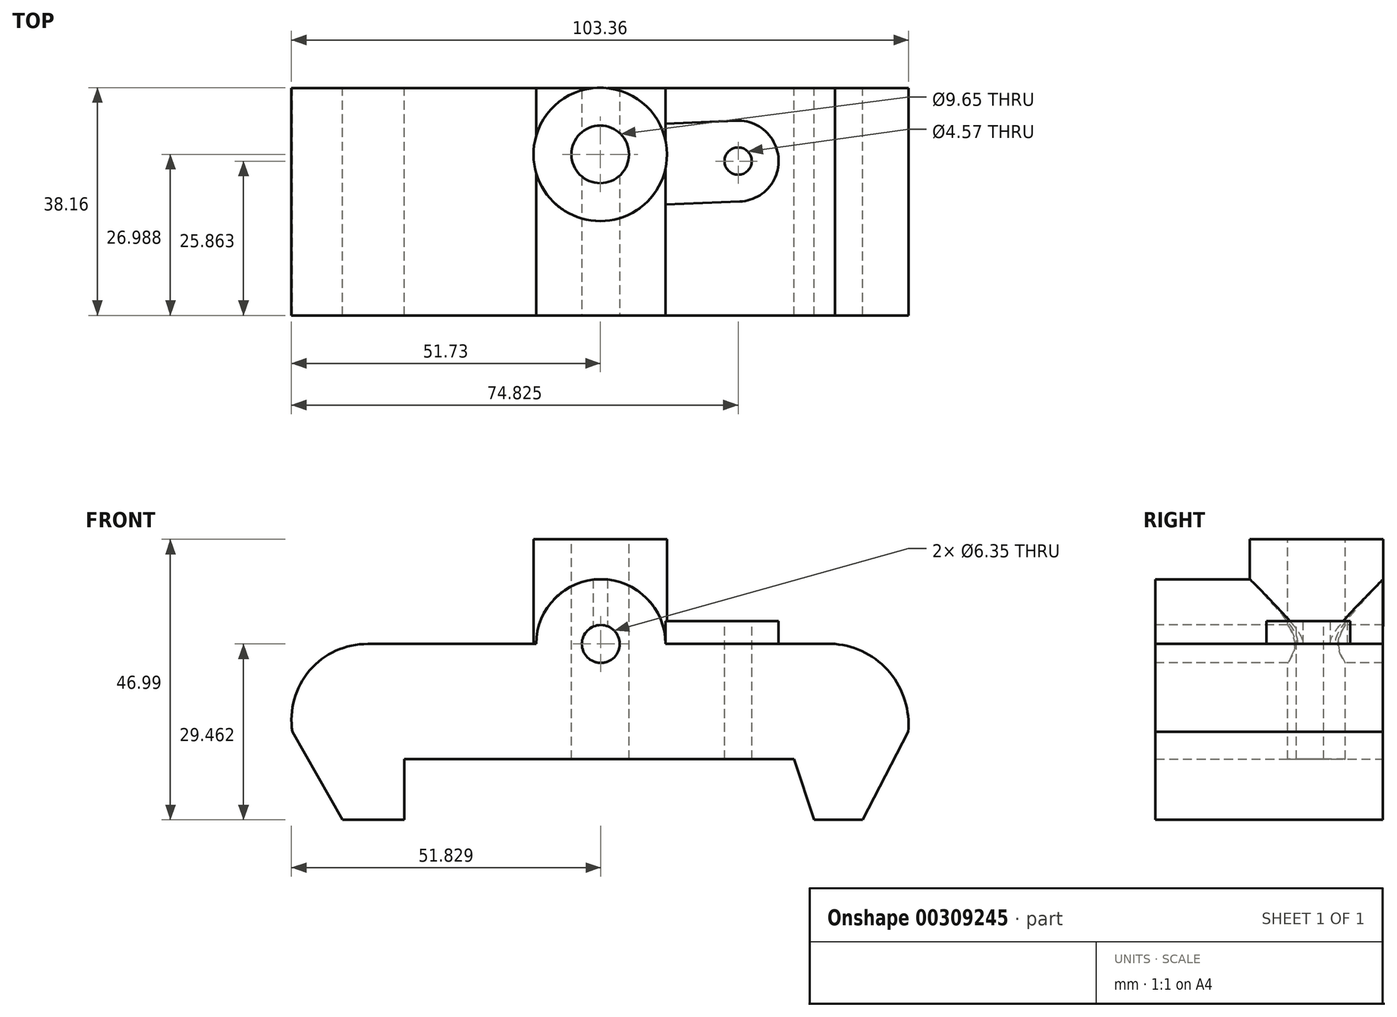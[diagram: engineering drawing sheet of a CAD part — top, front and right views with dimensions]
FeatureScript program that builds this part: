
annotation { "Feature Type Name" : "Feature", "Feature Type Description" : "" }
export const myFeature = defineFeature(function(context is Context, id is Id, definition is map)
    precondition{}
    {
        {
            var Q0;
            Q0=qCreatedBy(makeId("Front.planeOp"),FACE);
            var sketch = newSketch(context, id + "F0", { "sketchPlane" : qUnion([Q0])});
            skLineSegment(sketch, "E0.bottom", {"start": v(-43.18, -14.73) * mm, "end": v(-32.82, -14.73) * mm});
            skLineSegment(sketch, "E0.top", {"start": v(-39.11, 14.73) * mm, "end": v(-10.74, 14.73) * mm});
            skLineSegment(sketch, "E0.left", {"start": v(-51.56, 0) * mm, "end": v(-51.56, 4.06) * mm});
            skLineSegment(sketch, "E0.right", {"start": v(51.56, 0) * mm, "end": v(51.56, 2.62) * mm});
            skPoint(sketch, "E0.middle", {"position": v(0, 0) * mm});
            skArc(sketch, "E1", {"start": v(-38.94, 14.73) * mm, "mid": v(-48.67, 10.3) * mm, "end": v(-51.56, 0) * mm});
            skArc(sketch, "E2", {"start": v(51.56, 0) * mm, "mid": v(48.51, 9.92) * mm, "end": v(39.3, 14.73) * mm});
            skLineSegment(sketch, "E3", {"start": v(-51.56, 0) * mm, "end": v(-43.18, -14.73) * mm});
            skPoint(sketch, "E4.orphan", {"position": v(-51.56, 14.73) * mm});
            skPoint(sketch, "E5.orphan", {"position": v(-51.56, -14.73) * mm});
            skPoint(sketch, "E6.orphan", {"position": v(51.56, 14.73) * mm});
            skLineSegment(sketch, "E7", {"start": v(51.56, 0) * mm, "end": v(43.94, -14.73) * mm});
            skPoint(sketch, "E8.orphan", {"position": v(51.56, -14.73) * mm});
            skLineSegment(sketch, "E9.bottom", {"start": v(-32.82, -4.57) * mm, "end": v(32.46, -4.57) * mm});
            skLineSegment(sketch, "E9.left", {"start": v(-32.82, -4.57) * mm, "end": v(-32.82, -14.73) * mm});
            skPoint(sketch, "E10", {"position": v(-32.82, -14.73) * mm});
            skPoint(sketch, "E11", {"position": v(32.46, -14.73) * mm});
            skLineSegment(sketch, "E12.trimOffspring", {"start": v(35.81, -14.73) * mm, "end": v(43.94, -14.73) * mm});
            skLineSegment(sketch, "E13", {"start": v(32.46, -4.57) * mm, "end": v(35.81, -14.73) * mm});
            skArc(sketch, "E14", {"start": v(10.94, 14.73) * mm, "mid": v(0.1, 25.58) * mm, "end": v(-10.74, 14.73) * mm});
            skLineSegment(sketch, "E15.trimOffspring", {"start": v(10.94, 14.73) * mm, "end": v(39.3, 14.73) * mm});
            skSolve(sketch);
        }
        {
            var Q0;
            Q0 = qSketchRegion(id + "F0", true);
            extrude(context, id + "F1", {"entities" : qUnion([Q0]), "depth" : 38.1 * mm});
        }
        {
            var Q0;
            Q0=makeQuery(id+"F1.opExtrude","SWEPT_FACE",FACE,{"disambiguationData":[OSD([sQuery(id+"F0.wireOp",EDGE,"E0.top")])]});
            var sketch = newSketch(context, id + "F2", { "sketchPlane" : qUnion([Q0])});
            skCircle(sketch, "E16", {"center": v(0, -11.11) * mm, "radius": 11.18 * mm});
            skPoint(sketch, "E17", {"position": v(-24.84, -38.1) * mm});
            skSolve(sketch);
        }
        {
            var Q0;
            Q0 = qSketchRegion(id + "F2", true);
            extrude(context, id + "F3", {"entities" : qUnion([Q0]), "operationType" : NewBodyOperationType.ADD, "depth" : 17.53 * mm});
        }
        {
            var Q0;
            Q0=makeQuery(id+"F3.opExtrude","CAP_FACE",FACE,{"disambiguationData":[OSD([sQuery(id+"F2.wireOp",EDGE,"E16")])],"isStart":false});
            var sketch = newSketch(context, id + "F4", { "sketchPlane" : qUnion([Q0])});
            skPoint(sketch, "E18", {"position": v(0, -11.11) * mm});
            skSolve(sketch);
        }
        {
            var Q0;
            Q0=sQuery(id+"F4.wireOp",VERTEX,"E18");
            var Q1;
            Q1=makeQuery(id+"F1.opExtrude","SWEPT_BODY",BODY,{"disambiguationData":[OSD([sQuery(id+"F0.wireOp",EDGE,"E0.bottom"),sQuery(id+"F0.wireOp",EDGE,"E0.top"),sQuery(id+"F0.wireOp",EDGE,"E1"),sQuery(id+"F0.wireOp",EDGE,"E2"),sQuery(id+"F0.wireOp",EDGE,"E3"),sQuery(id+"F0.wireOp",EDGE,"E7"),sQuery(id+"F0.wireOp",EDGE,"E9.bottom"),sQuery(id+"F0.wireOp",EDGE,"E9.left"),sQuery(id+"F0.wireOp",EDGE,"E12.trimOffspring"),sQuery(id+"F0.wireOp",EDGE,"E13")])]});
            hole(context, id + "F5", {"style" : HoleStyle.SIMPLE, "endStyle" : HoleEndStyle.THROUGH, "holeDiameter" : 9.65 * mm, "tappedDepth" : 12.7 * mm, "tapClearance" : 3, "startFromSketch" : true, "locations" : qUnion([Q0]), "scope" : qUnion([Q1])});
        }
        {
            var Q0;
            Q0=makeQuery(id+"F1.opExtrude","SWEPT_FACE",FACE,{"disambiguationData":[OSD([sQuery(id+"F0.wireOp",EDGE,"E15.trimOffspring")])]});
            var sketch = newSketch(context, id + "F6", { "sketchPlane" : qUnion([Q0])});
            skArc(sketch, "E19", {"start": v(23.36, -19) * mm, "mid": v(29.86, -11.96) * mm, "end": v(22.8, -5.47) * mm});
            skLineSegment(sketch, "E20", {"start": v(22.8, -5.47) * mm, "end": v(10.94, -5.98) * mm});
            skLineSegment(sketch, "E21", {"start": v(23.36, -19) * mm, "end": v(10.94, -19.5) * mm});
            skSolve(sketch);
        }
        {
            var Q0;
            Q0=makeQuery(id+"F6.imprint","IMPRINT",FACE,{"disambiguationData":[TD([[makeQuery(id+"F6.imprint","IMPRINT",EDGE,{"derivedFrom":sQuery(id+"F6.wireOp",EDGE,"E19")}),1.0]])]});
            extrude(context, id + "F7", {"entities" : qUnion([Q0]), "operationType" : NewBodyOperationType.ADD, "depth" : 3.8 * mm});
        }
        {
            var Q0;
            Q0=makeQuery(id+"F7.opExtrude","CAP_FACE",FACE,{"disambiguationData":[OSD([sQuery(id+"F0.wireOp",EDGE,"E14"),sQuery(id+"F0.wireOp",EDGE,"E15.trimOffspring"),sQuery(id+"F2.wireOp",EDGE,"E16"),sQuery(id+"F6.wireOp",EDGE,"E19"),sQuery(id+"F6.wireOp",EDGE,"E20"),sQuery(id+"F6.wireOp",EDGE,"E21")])],"isStart":false});
            var sketch = newSketch(context, id + "F8", { "sketchPlane" : qUnion([Q0])});
            skPoint(sketch, "E22", {"position": v(23.1, -12.24) * mm});
            skSolve(sketch);
        }
        {
            var Q0;
            Q0=sQuery(id+"F8.wireOp",VERTEX,"E22");
            var Q1;
            Q1=makeQuery(id+"F1.opExtrude","SWEPT_BODY",BODY,{"disambiguationData":[OSD([sQuery(id+"F0.wireOp",EDGE,"E0.bottom"),sQuery(id+"F0.wireOp",EDGE,"E0.top"),sQuery(id+"F0.wireOp",EDGE,"E1"),sQuery(id+"F0.wireOp",EDGE,"E2"),sQuery(id+"F0.wireOp",EDGE,"E3"),sQuery(id+"F0.wireOp",EDGE,"E7"),sQuery(id+"F0.wireOp",EDGE,"E9.bottom"),sQuery(id+"F0.wireOp",EDGE,"E9.left"),sQuery(id+"F0.wireOp",EDGE,"E12.trimOffspring"),sQuery(id+"F0.wireOp",EDGE,"E13"),sQuery(id+"F0.wireOp",EDGE,"E14"),sQuery(id+"F0.wireOp",EDGE,"E15.trimOffspring")])]});
            hole(context, id + "F9", {"style" : HoleStyle.SIMPLE, "endStyle" : HoleEndStyle.THROUGH, "holeDiameter" : 4.57 * mm, "tappedDepth" : 12.7 * mm, "tapClearance" : 3, "startFromSketch" : true, "locations" : qUnion([Q0]), "scope" : qUnion([Q1])});
        }
        {
            var Q0;
            Q0=makeQuery(id+"F1.opExtrude","CAP_FACE",FACE,{"disambiguationData":[OSD([sQuery(id+"F0.wireOp",EDGE,"E0.bottom"),sQuery(id+"F0.wireOp",EDGE,"E0.top"),sQuery(id+"F0.wireOp",EDGE,"E1"),sQuery(id+"F0.wireOp",EDGE,"E2"),sQuery(id+"F0.wireOp",EDGE,"E3"),sQuery(id+"F0.wireOp",EDGE,"E7"),sQuery(id+"F0.wireOp",EDGE,"E9.bottom"),sQuery(id+"F0.wireOp",EDGE,"E9.left"),sQuery(id+"F0.wireOp",EDGE,"E12.trimOffspring"),sQuery(id+"F0.wireOp",EDGE,"E13"),sQuery(id+"F0.wireOp",EDGE,"E14"),sQuery(id+"F0.wireOp",EDGE,"E15.trimOffspring")])],"isStart":false});
            var sketch = newSketch(context, id + "F10", { "sketchPlane" : qUnion([Q0])});
            skPoint(sketch, "E23", {"position": v(0.1, 14.73) * mm});
            skSolve(sketch);
        }
        {
            var Q0;
            Q0=sQuery(id+"F10.wireOp",VERTEX,"E23");
            var Q1;
            Q1=makeQuery(id+"F1.opExtrude","SWEPT_BODY",BODY,{"disambiguationData":[OSD([sQuery(id+"F0.wireOp",EDGE,"E0.bottom"),sQuery(id+"F0.wireOp",EDGE,"E0.top"),sQuery(id+"F0.wireOp",EDGE,"E1"),sQuery(id+"F0.wireOp",EDGE,"E2"),sQuery(id+"F0.wireOp",EDGE,"E3"),sQuery(id+"F0.wireOp",EDGE,"E7"),sQuery(id+"F0.wireOp",EDGE,"E9.bottom"),sQuery(id+"F0.wireOp",EDGE,"E9.left"),sQuery(id+"F0.wireOp",EDGE,"E12.trimOffspring"),sQuery(id+"F0.wireOp",EDGE,"E13"),sQuery(id+"F0.wireOp",EDGE,"E14"),sQuery(id+"F0.wireOp",EDGE,"E15.trimOffspring")])]});
            hole(context, id + "F11", {"style" : HoleStyle.SIMPLE, "endStyle" : HoleEndStyle.THROUGH, "holeDiameter" : 6.35 * mm, "tappedDepth" : 12.7 * mm, "tapClearance" : 3, "startFromSketch" : true, "locations" : qUnion([Q0]), "scope" : qUnion([Q1])});
        }
    });
